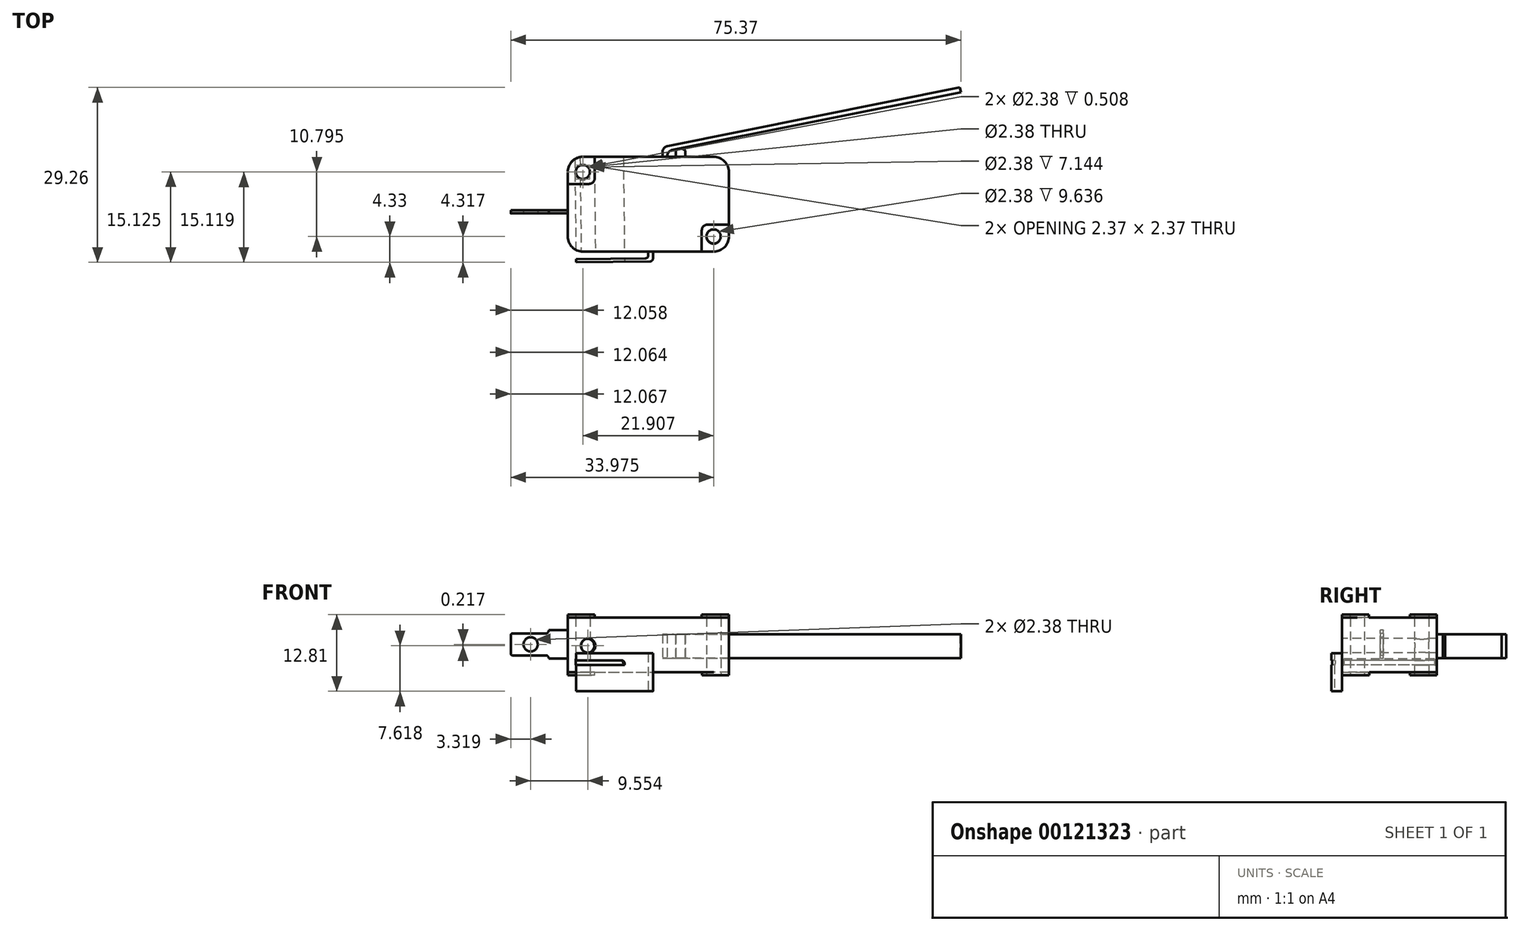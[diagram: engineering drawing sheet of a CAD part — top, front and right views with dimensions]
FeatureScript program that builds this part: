
annotation { "Feature Type Name" : "Feature", "Feature Type Description" : "" }
export const myFeature = defineFeature(function(context is Context, id is Id, definition is map)
    precondition{}
    {
        {
            var Q0;
            Q0=qCreatedBy(makeId("Top.planeOp"),FACE);
            var sketch = newSketch(context, id + "F0", { "sketchPlane" : qUnion([Q0])});
            skLineSegment(sketch, "E0.bottom", {"start": v(-22.21, 9.46) * mm, "end": v(-0.3, 9.46) * mm});
            skLineSegment(sketch, "E0.top", {"start": v(-22.21, -6.42) * mm, "end": v(-0.3, -6.42) * mm});
            skLineSegment(sketch, "E0.left", {"start": v(-24.75, 6.92) * mm, "end": v(-24.75, -3.88) * mm});
            skLineSegment(sketch, "E0.right", {"start": v(2.23, 6.92) * mm, "end": v(2.23, -3.88) * mm});
            skPoint(sketch, "E1.visualSharp", {"position": v(-24.75, 9.46) * mm});
            skArc(sketch, "E1.filletArc", {"start": v(-22.21, 9.46) * mm, "mid": v(-24, 8.71) * mm, "end": v(-24.75, 6.92) * mm});
            skPoint(sketch, "E2.visualSharp", {"position": v(2.23, 9.46) * mm});
            skArc(sketch, "E2.filletArc", {"start": v(2.23, 6.92) * mm, "mid": v(1.5, 8.71) * mm, "end": v(-0.3, 9.46) * mm});
            skPoint(sketch, "E3.visualSharp", {"position": v(2.23, -6.42) * mm});
            skArc(sketch, "E3.filletArc", {"start": v(-0.3, -6.42) * mm, "mid": v(1.5, -5.68) * mm, "end": v(2.23, -3.88) * mm});
            skPoint(sketch, "E4.visualSharp", {"position": v(-24.75, -6.42) * mm});
            skArc(sketch, "E4.filletArc", {"start": v(-24.75, -3.88) * mm, "mid": v(-24, -5.68) * mm, "end": v(-22.21, -6.42) * mm});
            skCircle(sketch, "E5", {"center": v(-22.21, 6.92) * mm, "radius": 1.2 * mm});
            skCircle(sketch, "E6", {"center": v(-0.3, -3.88) * mm, "radius": 1.2 * mm});
            skSolve(sketch);
        }
        {
            var Q0;
            Q0=qSketchRegion(id+"F0",true);
            extrude(context, id + "F1", {"entities" : qUnion([Q0]), "depth" : 9.13 * mm});
        }
        {
            var Q0;
            Q0=makeQuery(id+"F1.opExtrude","CAP_FACE",FACE,{"disambiguationData":[OSD([sQuery(id+"F0.wireOp",EDGE,"E0.bottom"),sQuery(id+"F0.wireOp",EDGE,"E0.top"),sQuery(id+"F0.wireOp",EDGE,"E0.left"),sQuery(id+"F0.wireOp",EDGE,"E0.right"),sQuery(id+"F0.wireOp",EDGE,"E1.filletArc"),sQuery(id+"F0.wireOp",EDGE,"E2.filletArc"),sQuery(id+"F0.wireOp",EDGE,"E3.filletArc"),sQuery(id+"F0.wireOp",EDGE,"E4.filletArc"),sQuery(id+"F0.wireOp",EDGE,"E5"),sQuery(id+"F0.wireOp",EDGE,"E6")])],"isStart":true});
            cPlane(context, id + "F2", {"entities" : qUnion([Q0]), "cplaneType" : CPlaneType.OFFSET, "offset" : 2.38 * mm, "oppositeDirection" : true, "width" : 152.4 * mm, "height" : 152.4 * mm});
        }
        {
            var Q0;
            Q0=qCreatedBy(id+"F2.planeOp",FACE);
            var sketch = newSketch(context, id + "F3", { "sketchPlane" : qUnion([Q0])});
            skLineSegment(sketch, "E7", {"start": v(-8.88, -9.48) * mm, "end": v(-8.88, -11.07) * mm});
            skLineSegment(sketch, "E8", {"start": v(-8.88, -11.07) * mm, "end": v(40.93, -21.05) * mm});
            skLineSegment(sketch, "E9", {"start": v(40.93, -21.05) * mm, "end": v(41.09, -20.28) * mm});
            skLineSegment(sketch, "E10", {"start": v(41.09, -20.28) * mm, "end": v(-8.08, -10.42) * mm});
            skLineSegment(sketch, "E11", {"start": v(-8.08, -10.42) * mm, "end": v(-8.08, -9.48) * mm});
            skLineSegment(sketch, "E12", {"start": v(-8.08, -9.48) * mm, "end": v(-8.88, -9.48) * mm});
            skSolve(sketch);
        }
        {
            var Q0;
            Q0=qSketchRegion(id+"F3",true);
            extrude(context, id + "F4", {"entities" : qUnion([Q0]), "oppositeDirection" : true, "depth" : 3.97 * mm});
        }
        {
            var Q0;
            Q0=makeQuery(id+"F4.opExtrude","SWEPT_EDGE",EDGE,{"disambiguationData":[OSD([sQuery(id+"F3.wireOp",EDGE,"E7"),sQuery(id+"F3.wireOp",EDGE,"E8")])]});
            var Q1;
            Q1=makeQuery(id+"F4.opExtrude","SWEPT_EDGE",EDGE,{"disambiguationData":[OSD([sQuery(id+"F3.wireOp",EDGE,"E10"),sQuery(id+"F3.wireOp",EDGE,"E11")])]});
            fillet(context, id + "F5", {"entities" : qUnion([Q0, Q1]), "radius" : 1.02 * mm, "tangentPropagation" : true, "allowEdgeOverflow" : false});
        }
        {
            var Q0;
            Q0=makeQuery(id+"F1.opExtrude","CAP_FACE",FACE,{"disambiguationData":[OSD([sQuery(id+"F0.wireOp",EDGE,"E0.bottom"),sQuery(id+"F0.wireOp",EDGE,"E0.top"),sQuery(id+"F0.wireOp",EDGE,"E0.left"),sQuery(id+"F0.wireOp",EDGE,"E0.right"),sQuery(id+"F0.wireOp",EDGE,"E1.filletArc"),sQuery(id+"F0.wireOp",EDGE,"E2.filletArc"),sQuery(id+"F0.wireOp",EDGE,"E3.filletArc"),sQuery(id+"F0.wireOp",EDGE,"E4.filletArc"),sQuery(id+"F0.wireOp",EDGE,"E5"),sQuery(id+"F0.wireOp",EDGE,"E6")])],"isStart":false});
            var sketch = newSketch(context, id + "F6", { "sketchPlane" : qUnion([Q0])});
            skLineSegment(sketch, "E13.bottom", {"start": v(-22.22, 9.44) * mm, "end": v(-20.24, 9.44) * mm});
            skLineSegment(sketch, "E13.top", {"start": v(-2.3, -6.43) * mm, "end": v(-0.31, -6.43) * mm});
            skLineSegment(sketch, "E13.left", {"start": v(-24.76, 6.9) * mm, "end": v(-24.76, 4.92) * mm});
            skLineSegment(sketch, "E13.right", {"start": v(2.23, -1.9) * mm, "end": v(2.23, -3.9) * mm});
            skPoint(sketch, "E14.visualSharp", {"position": v(-24.76, 9.44) * mm});
            skArc(sketch, "E14.filletArc", {"start": v(-22.22, 9.44) * mm, "mid": v(-24.02, 8.7) * mm, "end": v(-24.76, 6.9) * mm});
            skPoint(sketch, "E15.visualSharp", {"position": v(2.23, 9.44) * mm});
            skPoint(sketch, "E16.visualSharp", {"position": v(2.23, -6.43) * mm});
            skArc(sketch, "E16.filletArc", {"start": v(-0.31, -6.43) * mm, "mid": v(1.48, -5.69) * mm, "end": v(2.23, -3.9) * mm});
            skPoint(sketch, "E17.visualSharp", {"position": v(-24.76, -6.43) * mm});
            skCircle(sketch, "E18", {"center": v(-22.22, 6.9) * mm, "radius": 1.2 * mm});
            skCircle(sketch, "E19", {"center": v(-0.31, -3.9) * mm, "radius": 1.2 * mm});
            skLineSegment(sketch, "E20.bottom", {"start": v(-1.37, -1.9) * mm, "end": v(2.23, -1.9) * mm});
            skLineSegment(sketch, "E20.left", {"start": v(-2.3, -2.84) * mm, "end": v(-2.3, -6.43) * mm});
            skLineSegment(sketch, "E21.top", {"start": v(-24.76, 4.92) * mm, "end": v(-21.17, 4.92) * mm});
            skLineSegment(sketch, "E21.right", {"start": v(-20.24, 9.44) * mm, "end": v(-20.24, 5.85) * mm});
            skPoint(sketch, "E22.visualSharp", {"position": v(-20.24, 4.92) * mm});
            skArc(sketch, "E22.filletArc", {"start": v(-21.17, 4.92) * mm, "mid": v(-20.51, 5.2) * mm, "end": v(-20.24, 5.85) * mm});
            skPoint(sketch, "E23.visualSharp", {"position": v(-2.3, -1.9) * mm});
            skArc(sketch, "E23.filletArc", {"start": v(-1.37, -1.9) * mm, "mid": v(-2.03, -2.18) * mm, "end": v(-2.3, -2.84) * mm});
            skSolve(sketch);
        }
        {
            var Q0;
            Q0=qSketchRegion(id+"F6",true);
            extrude(context, id + "F7", {"entities" : qUnion([Q0]), "operationType" : NewBodyOperationType.ADD, "depth" : 0.5 * mm});
        }
        {
            var Q0;
            Q0=qCreatedBy(id+"F2.planeOp",FACE);
            var sketch = newSketch(context, id + "F8", { "sketchPlane" : qUnion([Q0])});
            skLineSegment(sketch, "E24.bottom", {"start": v(-5.04, -9.44) * mm, "end": v(-6.67, -9.44) * mm});
            skLineSegment(sketch, "E24.top", {"start": v(-5.04, -10.44) * mm, "end": v(-6.67, -10.44) * mm});
            skLineSegment(sketch, "E24.left", {"start": v(-5.04, -9.44) * mm, "end": v(-5.04, -10.44) * mm});
            skLineSegment(sketch, "E24.right", {"start": v(-6.67, -9.44) * mm, "end": v(-6.67, -10.44) * mm});
            skArc(sketch, "E25", {"start": v(-6.67, -10.44) * mm, "mid": v(-5.86, -10.82) * mm, "end": v(-5.04, -10.44) * mm});
            skSolve(sketch);
        }
        {
            var Q0;
            Q0=qSketchRegion(id+"F8",true);
            extrude(context, id + "F9", {"entities" : qUnion([Q0]), "operationType" : NewBodyOperationType.ADD, "oppositeDirection" : true, "depth" : 3.97 * mm});
        }
        {
            var Q0;
            Q0=qCreatedBy(makeId("Top.planeOp"),FACE);
            cPlane(context, id + "F10", {"entities" : qUnion([Q0]), "cplaneType" : CPlaneType.OFFSET, "offset" : 2.75 / 406.4 * mm, "width" : 152.4 * mm, "height" : 152.4 * mm});
        }
        {
            var Q0;
            Q0=qCreatedBy(id+"F10.planeOp",FACE);
            var sketch = newSketch(context, id + "F11", { "sketchPlane" : qUnion([Q0])});
            skLineSegment(sketch, "E26", {"start": v(-11.26, -6.43) * mm, "end": v(-11.26, -7.55) * mm});
            skLineSegment(sketch, "E27", {"start": v(-23.36, -8.2) * mm, "end": v(-23.36, -7.7) * mm});
            skLineSegment(sketch, "E28", {"start": v(-23.36, -8.2) * mm, "end": v(-10.47, -8.05) * mm});
            skLineSegment(sketch, "E29", {"start": v(-10.47, -8.05) * mm, "end": v(-10.47, -6.43) * mm});
            skLineSegment(sketch, "E30", {"start": v(-11.26, -6.43) * mm, "end": v(-10.47, -6.43) * mm});
            skLineSegment(sketch, "E31", {"start": v(-10.47, -7.55) * mm, "end": v(-10.47, -6.43) * mm});
            skLineSegment(sketch, "E32", {"start": v(-23.36, -7.7) * mm, "end": v(-11.26, -7.55) * mm});
            skSolve(sketch);
        }
        {
            var Q0;
            Q0=makeQuery(id+"F11.imprint","IMPRINT",FACE,{"disambiguationData":[TD([[makeQuery(id+"F11.imprint","IMPRINT",EDGE,{"derivedFrom":sQuery(id+"F11.wireOp",EDGE,"E26")}),1.0]])]});
            extrude(context, id + "F12", {"entities" : qUnion([Q0]), "depth" : 3.17 * mm, "hasSecondDirection" : true, "secondDirectionOppositeDirection" : true, "secondDirectionDepth" : 3.17 * mm});
        }
        {
            var Q0;
            {var subQ0=sQuery(id+"F11.wireOp",EDGE,"E28");Q0=makeQuery(id+"FmFe5163YoJR6j5_2.boolean.opBoolean","MERGE",FACE,{"derivedFrom":[makeQuery(id+"F12.opExtrude","SWEPT_FACE",FACE,{"disambiguationData":[OSD([subQ0])]}),makeQuery(id+"FmFe5163YoJR6j5_2.opExtrude","SWEPT_FACE",FACE,{"disambiguationData":[OSD([subQ0])]})]});}
            var sketch = newSketch(context, id + "F13", { "sketchPlane" : qUnion([Q0])});
            skCircle(sketch, "E33", {"center": v(-22.31, 4.41) * mm, "radius": 0.82 * mm});
            skSolve(sketch);
        }
        {
            var Q0;
            Q0=makeQuery(id+"F13.imprint","IMPRINT",FACE,{"disambiguationData":[TD([[makeQuery(id+"F13.imprint","IMPRINT",EDGE,{"derivedFrom":sQuery(id+"F13.wireOp",EDGE,"E33")}),1.0]])]});
            extrude(context, id + "F14", {"entities" : qUnion([Q0]), "operationType" : NewBodyOperationType.REMOVE, "oppositeDirection" : true, "depth" : 0.5 * mm});
        }
        {
            var Q0;
            Q0=qCreatedBy(makeId("Front.planeOp"),FACE);
            cPlane(context, id + "F15", {"entities" : qUnion([Q0]), "cplaneType" : CPlaneType.OFFSET, "offset" : 0.03 * mm, "width" : 152.4 * mm, "height" : 152.4 * mm});
        }
        {
            var Q0;
            Q0=qCreatedBy(id+"F15.planeOp",FACE);
            var sketch = newSketch(context, id + "F16", { "sketchPlane" : qUnion([Q0])});
            skLineSegment(sketch, "E34", {"start": v(-24.75, 2.28) * mm, "end": v(-24.75, 7.05) * mm});
            skLineSegment(sketch, "E35", {"start": v(-24.75, 7.05) * mm, "end": v(-27.93, 7.05) * mm});
            skLineSegment(sketch, "E36", {"start": v(-34.28, 6.24) * mm, "end": v(-34.28, 3.1) * mm});
            skLineSegment(sketch, "E37", {"start": v(-27.93, 2.28) * mm, "end": v(-24.75, 2.28) * mm});
            skCircle(sketch, "E38", {"center": v(-30.96, 4.66) * mm, "radius": 1.2 * mm});
            skPoint(sketch, "E39", {"position": v(-34.28, 4.66) * mm});
            skLineSegment(sketch, "E40", {"start": v(-27.93, 7.05) * mm, "end": v(-27.93, 6.5) * mm});
            skLineSegment(sketch, "E41", {"start": v(-27.93, 2.84) * mm, "end": v(-27.93, 2.28) * mm});
            skLineSegment(sketch, "E42", {"start": v(-27.93, 6.5) * mm, "end": v(-34.02, 6.5) * mm});
            skLineSegment(sketch, "E43", {"start": v(-27.93, 2.84) * mm, "end": v(-34.02, 2.84) * mm});
            skPoint(sketch, "E44.newPointB", {"position": v(-34.28, 7.05) * mm});
            skArc(sketch, "E44.filletArc", {"start": v(-34.02, 6.5) * mm, "mid": v(-34.2, 6.42) * mm, "end": v(-34.28, 6.24) * mm});
            skPoint(sketch, "E45.newPointB", {"position": v(-34.28, 2.28) * mm});
            skArc(sketch, "E45.filletArc", {"start": v(-34.28, 3.1) * mm, "mid": v(-34.2, 2.91) * mm, "end": v(-34.02, 2.84) * mm});
            skSolve(sketch);
        }
        {
            var Q0;
            Q0=makeQuery(id+"F16.imprint","IMPRINT",FACE,{"disambiguationData":[TD([[makeQuery(id+"F16.imprint","IMPRINT",EDGE,{"derivedFrom":sQuery(id+"F16.wireOp",EDGE,"E34")}),1.0]])]});
            extrude(context, id + "F17", {"entities" : qUnion([Q0]), "oppositeDirection" : true, "depth" : 0.5 * mm});
        }
        {
            var Q0;
            Q0=makeQuery(id+"F12.opExtrude","SWEPT_FACE",FACE,{"disambiguationData":[OSD([sQuery(id+"F11.wireOp",EDGE,"E28")])]});
            var sketch = newSketch(context, id + "F18", { "sketchPlane" : qUnion([Q0])});
            skCircle(sketch, "E46", {"center": v(-21.39, 4.45) * mm, "radius": 1.2 * mm});
            skLineSegment(sketch, "E47", {"start": v(-15.32, 7.54) * mm, "end": v(-15.32, 6.75) * mm});
            skLineSegment(sketch, "E48", {"start": v(-15.32, 1.98) * mm, "end": v(-15.32, 1.2) * mm});
            skLineSegment(sketch, "E49", {"start": v(-15.32, 6.75) * mm, "end": v(-23.2, 6.75) * mm});
            skLineSegment(sketch, "E50", {"start": v(-15.32, 1.98) * mm, "end": v(-23.2, 1.98) * mm});
            skLineSegment(sketch, "E51", {"start": v(-23.45, 6.75) * mm, "end": v(-23.45, 7.54) * mm});
            skLineSegment(sketch, "E52", {"start": v(-23.45, 7.54) * mm, "end": v(-15.32, 7.54) * mm});
            skLineSegment(sketch, "E53", {"start": v(-23.45, 1.98) * mm, "end": v(-23.45, 1.2) * mm});
            skLineSegment(sketch, "E54", {"start": v(-23.45, 1.2) * mm, "end": v(-15.32, 1.2) * mm});
            skLineSegment(sketch, "E55", {"start": v(-23.45, 6.5) * mm, "end": v(-23.45, 2.24) * mm});
            skPoint(sketch, "E56.visualSharp", {"position": v(-23.45, 6.75) * mm});
            skArc(sketch, "E56.filletArc", {"start": v(-23.2, 6.75) * mm, "mid": v(-23.38, 6.67) * mm, "end": v(-23.45, 6.5) * mm});
            skPoint(sketch, "E57.visualSharp", {"position": v(-23.45, 1.98) * mm});
            skArc(sketch, "E57.filletArc", {"start": v(-23.45, 2.24) * mm, "mid": v(-23.38, 2.06) * mm, "end": v(-23.2, 1.98) * mm});
            skSolve(sketch);
        }
        {
            var Q0;
            Q0=qSketchRegion(id+"F18",true);
            var Q1;
            Q1=makeQuery(id+"F18.imprint","IMPRINT",FACE,{"disambiguationData":[TD([[makeQuery(id+"F18.imprint","IMPRINT",EDGE,{"derivedFrom":sQuery(id+"F18.wireOp",EDGE,"E47")}),-1.0]])]});
            var Q2;
            Q2=makeQuery(id+"F18.imprint","IMPRINT",FACE,{"disambiguationData":[TD([[makeQuery(id+"F18.imprint","IMPRINT",EDGE,{"derivedFrom":sQuery(id+"F18.wireOp",EDGE,"E48")}),-1.0]])]});
            extrude(context, id + "F19", {"entities" : qUnion([Q0, Q1, Q2]), "operationType" : NewBodyOperationType.REMOVE, "oppositeDirection" : true, "depth" : 25.4 * mm});
        }
        {
            var Q0;
            Q0=makeQuery(id+"F19.boolean.opBoolean","COPY",EDGE,{"derivedFrom":makeQuery(id+"F19.opExtrude","SWEPT_EDGE",EDGE,{"disambiguationData":[OSD([sQuery(id+"F18.wireOp",EDGE,"E47"),sQuery(id+"F18.wireOp",EDGE,"E49")])]})});
            var Q1;
            Q1=makeQuery(id+"F19.boolean.opBoolean","COPY",EDGE,{"derivedFrom":makeQuery(id+"F19.opExtrude","SWEPT_EDGE",EDGE,{"disambiguationData":[OSD([sQuery(id+"F18.wireOp",EDGE,"E48"),sQuery(id+"F18.wireOp",EDGE,"E50")])]})});
            var Q2;
            Q2=makeQuery(id+"F12.opExtrude","SWEPT_EDGE",EDGE,{"disambiguationData":[OSD([sQuery(id+"F11.wireOp",EDGE,"E28"),sQuery(id+"F11.wireOp",EDGE,"E29")])]});
            var Q3;
            Q3=makeQuery(id+"F12.opExtrude","SWEPT_EDGE",EDGE,{"disambiguationData":[OSD([sQuery(id+"F11.wireOp",EDGE,"E26"),sQuery(id+"F11.wireOp",EDGE,"E32")])]});
            fillet(context, id + "F20", {"entities" : qUnion([Q0, Q1, Q2, Q3]), "radius" : 0.5 * mm, "tangentPropagation" : true, "allowEdgeOverflow" : false});
        }
        {
            var Q0;
            Q0=makeQuery(id+"F17.opExtrude","SWEPT_EDGE",EDGE,{"disambiguationData":[OSD([sQuery(id+"F16.wireOp",EDGE,"E40"),sQuery(id+"F16.wireOp",EDGE,"E42")])]});
            var Q1;
            Q1=makeQuery(id+"F17.opExtrude","SWEPT_EDGE",EDGE,{"disambiguationData":[OSD([sQuery(id+"F16.wireOp",EDGE,"E41"),sQuery(id+"F16.wireOp",EDGE,"E43")])]});
            fillet(context, id + "F21", {"entities" : qUnion([Q0, Q1]), "radius" : 0.5 * mm, "tangentPropagation" : true, "allowEdgeOverflow" : false});
        }
        {
            var Q0;
            Q0=makeQuery(id+"F1.opExtrude","CAP_FACE",FACE,{"disambiguationData":[OSD([sQuery(id+"F0.wireOp",EDGE,"E0.bottom"),sQuery(id+"F0.wireOp",EDGE,"E0.top"),sQuery(id+"F0.wireOp",EDGE,"E0.left"),sQuery(id+"F0.wireOp",EDGE,"E0.right"),sQuery(id+"F0.wireOp",EDGE,"E1.filletArc"),sQuery(id+"F0.wireOp",EDGE,"E2.filletArc"),sQuery(id+"F0.wireOp",EDGE,"E3.filletArc"),sQuery(id+"F0.wireOp",EDGE,"E4.filletArc"),sQuery(id+"F0.wireOp",EDGE,"E5"),sQuery(id+"F0.wireOp",EDGE,"E6")])],"isStart":true});
            var sketch = newSketch(context, id + "F22", { "sketchPlane" : qUnion([Q0])});
            skPoint(sketch, "E58.visualSharp", {"position": v(19.76, 6.42) * mm});
            skPoint(sketch, "E59.visualSharp", {"position": v(-6.83, -9.46) * mm});
            skArc(sketch, "E60.MirrorCS", {"start": v(-22.21, -9.46) * mm, "mid": v(-24, -8.71) * mm, "end": v(-24.75, -6.92) * mm});
            skLineSegment(sketch, "E61.MirrorCS", {"start": v(-24.75, -4.93) * mm, "end": v(-24.75, -6.92) * mm});
            skLineSegment(sketch, "E62.MirrorCS", {"start": v(-21.16, -4.93) * mm, "end": v(-24.75, -4.93) * mm});
            skArc(sketch, "E63.MirrorCS", {"start": v(-21.16, -4.93) * mm, "mid": v(-20.5, -5.2) * mm, "end": v(-20.23, -5.86) * mm});
            skLineSegment(sketch, "E64.MirrorCS", {"start": v(-20.23, -5.86) * mm, "end": v(-20.23, -9.46) * mm});
            skLineSegment(sketch, "E65.MirrorCS", {"start": v(-20.23, -9.46) * mm, "end": v(-22.21, -9.46) * mm});
            skCircle(sketch, "E66.MirrorC", {"center": v(-22.21, -6.92) * mm, "radius": 1.2 * mm});
            skSolve(sketch);
        }
        {
            var Q0;
            Q0=qSketchRegion(id+"F22",true);
            extrude(context, id + "F23", {"entities" : qUnion([Q0]), "operationType" : NewBodyOperationType.ADD, "depth" : 0.5 * mm});
        }
        {
            var Q0;
            Q0=makeQuery(id+"F1.opExtrude","CAP_FACE",FACE,{"disambiguationData":[OSD([sQuery(id+"F0.wireOp",EDGE,"E0.bottom"),sQuery(id+"F0.wireOp",EDGE,"E0.top"),sQuery(id+"F0.wireOp",EDGE,"E0.left"),sQuery(id+"F0.wireOp",EDGE,"E0.right"),sQuery(id+"F0.wireOp",EDGE,"E1.filletArc"),sQuery(id+"F0.wireOp",EDGE,"E2.filletArc"),sQuery(id+"F0.wireOp",EDGE,"E3.filletArc"),sQuery(id+"F0.wireOp",EDGE,"E4.filletArc"),sQuery(id+"F0.wireOp",EDGE,"E5"),sQuery(id+"F0.wireOp",EDGE,"E6")])],"isStart":true});
            var sketch = newSketch(context, id + "F24", { "sketchPlane" : qUnion([Q0])});
            skPoint(sketch, "E67.visualSharp", {"position": v(6.35, 6.41) * mm});
            skCircle(sketch, "E68.MirrorC", {"center": v(-0.3, 3.88) * mm, "radius": 1.2 * mm});
            skLineSegment(sketch, "E69.MirrorCS", {"start": v(-2.3, 6.42) * mm, "end": v(-2.29, 2.83) * mm});
            skArc(sketch, "E70.MirrorCS", {"start": v(-1.36, 1.9) * mm, "mid": v(-2.02, 2.17) * mm, "end": v(-2.29, 2.83) * mm});
            skLineSegment(sketch, "E71.MirrorCS", {"start": v(2.24, 1.9) * mm, "end": v(-1.36, 1.9) * mm});
            skLineSegment(sketch, "E72.MirrorCS", {"start": v(2.23, 3.88) * mm, "end": v(2.24, 1.9) * mm});
            skArc(sketch, "E73.MirrorCS", {"start": v(-0.3, 6.42) * mm, "mid": v(1.49, 5.68) * mm, "end": v(2.23, 3.88) * mm});
            skLineSegment(sketch, "E74.MirrorCS", {"start": v(-0.3, 6.42) * mm, "end": v(-2.3, 6.42) * mm});
            skSolve(sketch);
        }
        {
            var Q0;
            Q0=qSketchRegion(id+"F24",true);
            extrude(context, id + "F25", {"entities" : qUnion([Q0]), "operationType" : NewBodyOperationType.ADD, "depth" : 0.5 * mm});
        }
    });
